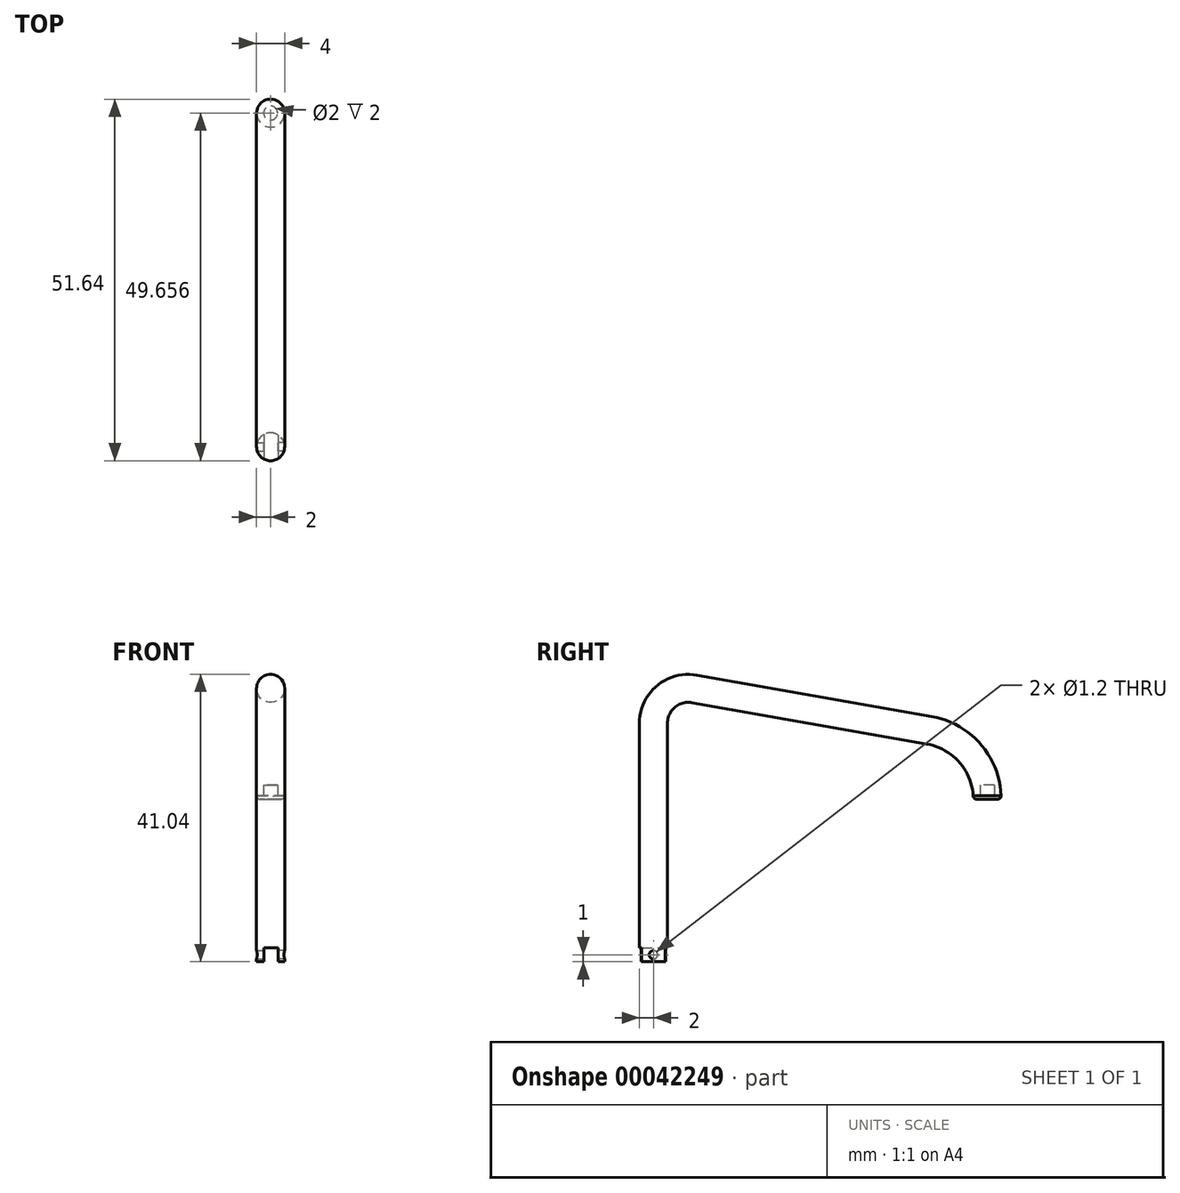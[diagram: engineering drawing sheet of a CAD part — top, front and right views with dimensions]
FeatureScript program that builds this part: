
annotation { "Feature Type Name" : "Feature", "Feature Type Description" : "" }
export const myFeature = defineFeature(function(context is Context, id is Id, definition is map)
    precondition{}
    {
        {
            var Q0;
            Q0=qCreatedBy(makeId("Top.planeOp"),FACE);
            var sketch = newSketch(context, id + "F0", { "sketchPlane" : qUnion([Q0])});
            skCircle(sketch, "E0", {"center": v(0, 0) * mm, "radius": 2 * mm});
            skSolve(sketch);
        }
        {
            var Q0;
            Q0=qCreatedBy(makeId("Right.planeOp"),FACE);
            var sketch = newSketch(context, id + "F1", { "sketchPlane" : qUnion([Q0])});
            skLineSegment(sketch, "E1", {"start": v(0, 0) * mm, "end": v(0, 4.04) * mm});
            skLineSegment(sketch, "E2", {"start": v(5.87, 8.97) * mm, "end": v(39.4, 3.05) * mm});
            skLineSegment(sketch, "E3", {"start": v(47.66, -6.8) * mm, "end": v(47.66, -8.4) * mm});
            skPoint(sketch, "E4.visualSharp", {"position": v(47.66, 1.6) * mm});
            skArc(sketch, "E4.filletArc", {"start": v(47.66, -6.8) * mm, "mid": v(45.32, -0.37) * mm, "end": v(39.4, 3.05) * mm});
            skPoint(sketch, "E5.visualSharp", {"position": v(0, 10) * mm});
            skArc(sketch, "E5.filletArc", {"start": v(5.87, 8.97) * mm, "mid": v(1.79, 7.87) * mm, "end": v(0, 4.04) * mm});
            skSolve(sketch);
        }
        {
            var Q0;
            Q0=makeQuery(id+"F0.imprint","IMPRINT",FACE,{"disambiguationData":[TD([[makeQuery(id+"F0.imprint","IMPRINT",EDGE,{"derivedFrom":sQuery(id+"F0.wireOp",EDGE,"E0")}),1.0]])]});
            var Q1;
            Q1=sQuery(id+"F1.wireOp",EDGE,"E4.filletArc");
            var Q2;
            Q2=sQuery(id+"F1.wireOp",EDGE,"E2");
            var Q3;
            Q3=sQuery(id+"F1.wireOp",EDGE,"E1");
            var Q4;
            Q4=sQuery(id+"F1.wireOp",EDGE,"E5.filletArc");
            sweep(context, id + "F2", {"profiles" : qUnion([Q0]), "path" : qUnion([Q1, Q2, Q3, Q4])});
        }
        {
            var Q0;
            Q0=makeQuery(id+"F2.opSweep","CAP_FACE",FACE,{"disambiguationData":[OSD([sQuery(id+"F0.wireOp",EDGE,"E0"),sQuery(id+"F1.wireOp",VERTEX,"E4.filletArc.start")])],"isStart":false});
            var sketch = newSketch(context, id + "F3", { "sketchPlane" : qUnion([Q0])});
            skCircle(sketch, "E6", {"center": v(0, -47.66) * mm, "radius": 1 * mm});
            skSolve(sketch);
        }
        {
            var Q0;
            Q0 = qSketchRegion(id + "F3", true);
            extrude(context, id + "F4", {"entities" : qUnion([Q0]), "operationType" : NewBodyOperationType.REMOVE, "oppositeDirection" : true, "depth" : 2 * mm});
        }
        {
            var Q0;
            Q0=makeQuery(id+"F2.opSweep","CAP_EDGE",EDGE,{"disambiguationData":[OSD([sQuery(id+"F0.wireOp",EDGE,"E0"),sQuery(id+"F1.wireOp",VERTEX,"E4.filletArc.start")])],"isStart":false});
            fillet(context, id + "F5", {"entities" : qUnion([Q0]), "radius" : 0.5 * mm, "tangentPropagation" : true, "allowEdgeOverflow" : false});
        }
        {
            var Q0;
            Q0=makeQuery(id+"F2.opSweep","CAP_FACE",FACE,{"disambiguationData":[OSD([sQuery(id+"F0.wireOp",EDGE,"E0"),sQuery(id+"F1.wireOp",VERTEX,"E1.start")])],"isStart":true});
            var sketch = newSketch(context, id + "F6", { "sketchPlane" : qUnion([Q0])});
            skCircle(sketch, "E7", {"center": v(0, 0) * mm, "radius": 2 * mm});
            skSolve(sketch);
        }
        {
            var Q0;
            Q0 = qSketchRegion(id + "F6", true);
            extrude(context, id + "F7", {"entities" : qUnion([Q0]), "operationType" : NewBodyOperationType.ADD, "depth" : 30 * mm});
        }
        {
            var Q0;
            Q0=qCreatedBy(makeId("Front.planeOp"),FACE);
            var sketch = newSketch(context, id + "F8", { "sketchPlane" : qUnion([Q0])});
            skLineSegment(sketch, "E8.bottom", {"start": v(-0.92, -28.02) * mm, "end": v(1.08, -28.02) * mm});
            skLineSegment(sketch, "E8.top", {"start": v(-0.92, -30.02) * mm, "end": v(1.08, -30.02) * mm});
            skLineSegment(sketch, "E8.left", {"start": v(-0.92, -28.02) * mm, "end": v(-0.92, -30.02) * mm});
            skLineSegment(sketch, "E8.right", {"start": v(1.08, -28.02) * mm, "end": v(1.08, -30.02) * mm});
            skSolve(sketch);
        }
        {
            var Q0;
            Q0 = qSketchRegion(id + "F8", true);
            extrude(context, id + "F9", {"entities" : qUnion([Q0]), "operationType" : NewBodyOperationType.REMOVE, "depth" : 50 * mm});
        }
        {
            var Q0;
            Q0=makeQuery(id+"F9.boolean.opBoolean","COPY",FACE,{"derivedFrom":makeQuery(id+"F9.opExtrude","CAP_FACE",FACE,{"disambiguationData":[OSD([sQuery(id+"F8.wireOp",EDGE,"E8.bottom"),sQuery(id+"F8.wireOp",EDGE,"E8.top"),sQuery(id+"F8.wireOp",EDGE,"E8.left"),sQuery(id+"F8.wireOp",EDGE,"E8.right")])],"isStart":true})});
            var sketch = newSketch(context, id + "F10", { "sketchPlane" : qUnion([Q0])});
            skLineSegment(sketch, "E9.bottom", {"start": v(-0.92, -28.02) * mm, "end": v(1.08, -28.02) * mm});
            skLineSegment(sketch, "E9.top", {"start": v(-0.92, -30) * mm, "end": v(1.08, -30) * mm});
            skLineSegment(sketch, "E9.left", {"start": v(-0.92, -28.02) * mm, "end": v(-0.92, -30) * mm});
            skLineSegment(sketch, "E9.right", {"start": v(1.08, -28.02) * mm, "end": v(1.08, -30) * mm});
            skSolve(sketch);
        }
        {
            var Q0;
            Q0 = qSketchRegion(id + "F10", true);
            extrude(context, id + "F11", {"entities" : qUnion([Q0]), "operationType" : NewBodyOperationType.REMOVE, "oppositeDirection" : true, "depth" : 25 * mm});
        }
        {
            var Q0;
            Q0=qCreatedBy(makeId("Right.planeOp"),FACE);
            var sketch = newSketch(context, id + "F12", { "sketchPlane" : qUnion([Q0])});
            skLineSegment(sketch, "E10", {"start": v(0, -29.08) * mm, "end": v(0, -28.92) * mm, "construction": true});
            skCircle(sketch, "E11", {"center": v(0, -29) * mm, "radius": 0.6 * mm});
            skSolve(sketch);
        }
        {
            var Q0;
            Q0 = qSketchRegion(id + "F12", true);
            extrude(context, id + "F13", {"entities" : qUnion([Q0]), "operationType" : NewBodyOperationType.REMOVE, "depth" : 4.55 * mm});
        }
        {
            var Q0;
            Q0=makeQuery(id+"F11.boolean.opBoolean","MERGE",FACE,{"derivedFrom":[makeQuery(id+"F9.boolean.opBoolean","COPY",FACE,{"derivedFrom":makeQuery(id+"F9.opExtrude","SWEPT_FACE",FACE,{"disambiguationData":[OSD([sQuery(id+"F8.wireOp",EDGE,"E8.left")])]})}),makeQuery(id+"F11.opExtrude","SWEPT_FACE",FACE,{"disambiguationData":[OSD([sQuery(id+"F10.wireOp",EDGE,"E9.left")])]})]});
            var sketch = newSketch(context, id + "F14", { "sketchPlane" : qUnion([Q0])});
            skLineSegment(sketch, "E12", {"start": v(0, -23.29) * mm, "end": v(0, -34.71) * mm});
            skCircle(sketch, "E13", {"center": v(0, -29) * mm, "radius": 0.6 * mm});
            skSolve(sketch);
        }
        {
            var Q0;
            Q0 = qSketchRegion(id + "F14", true);
            extrude(context, id + "F15", {"entities" : qUnion([Q0]), "operationType" : NewBodyOperationType.REMOVE, "oppositeDirection" : true, "depth" : 10 * mm});
        }
    });
